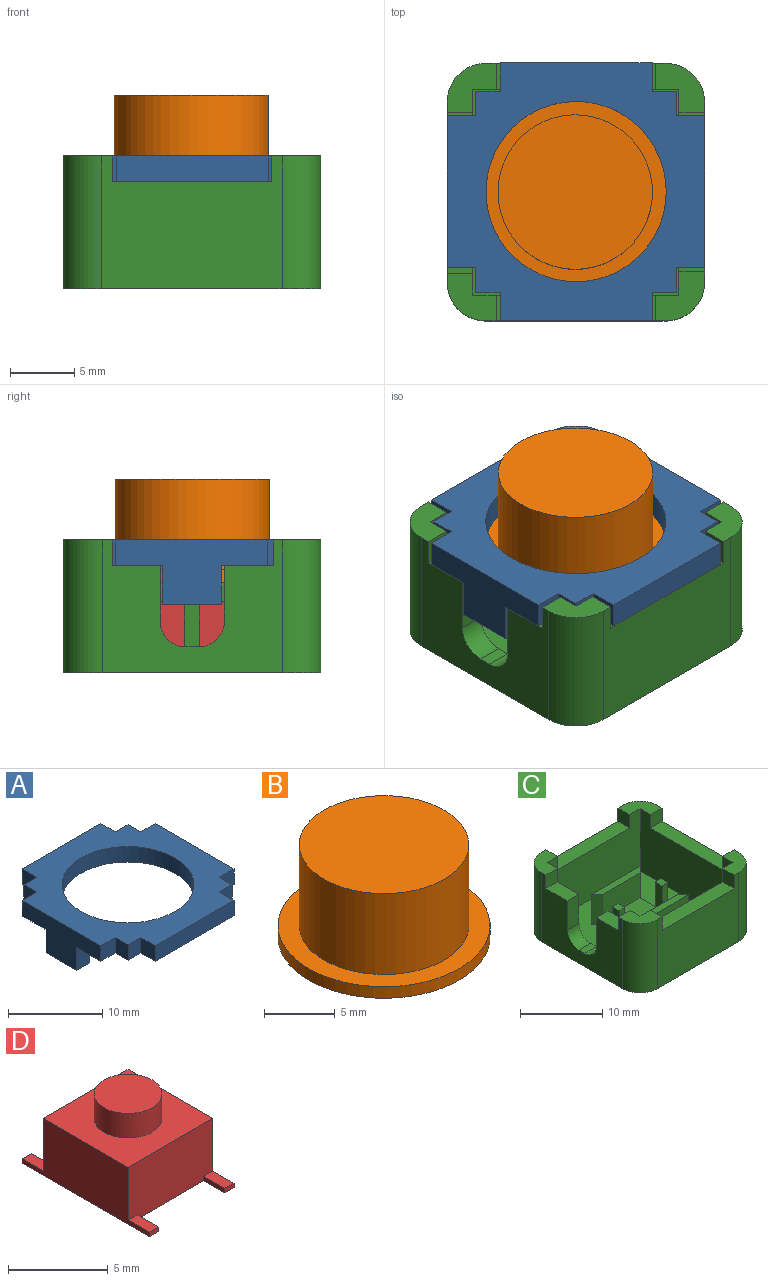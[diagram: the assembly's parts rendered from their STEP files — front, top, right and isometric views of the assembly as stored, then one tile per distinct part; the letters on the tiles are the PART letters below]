
ASSEMBLY  parts=4 mates=3
PART A: 27 faces, bbox 20x20x5 mm
  f0: plane 11.8x2mm, normal (0,1,0), area 23.6mm2, adj f4,f5,f18,f22
  f1: plane 11.8x5mm, normal (-1,0,0), area 37.4mm2, adj f4,f5,f13,f15,f23,f25,f26
  f2: plane 11.8x2mm, normal (0,-1,0), area 23.6mm2, adj f4,f5,f7,f14
  f3: plane 11.8x2mm, normal (1,0,0), area 23.6mm2, adj f4,f5,f8,f21
  f4: plane 20x20mm, normal (0,0,1), area 193.3mm2, adj f0,f1,f2,f3,f6,f7,f8,f9
  f5: plane 20x20mm, normal (0,0,-1), area 184.1mm2, adj f0,f1,f2,f3,f6,f7,f8,f9
  f6: cylinder r=7mm len=14mm, axis (0,0,-1), area 88mm2, adj f4,f5
  f7: plane 2.2x2mm, normal (1,0,0), area 4.4mm2, adj f2,f4,f5,f10
  f8: plane 2.2x2mm, normal (0,-1,0), area 4.4mm2, adj f3,f4,f5,f9
  f9: plane 2x1.9mm, normal (1,0,0), area 3.8mm2, adj f4,f5,f8,f10
  f10: plane 2x1.9mm, normal (0,-1,0), area 3.8mm2, adj f4,f5,f7,f9
  f11: plane 2x1.9mm, normal (0,-1,0), area 3.8mm2, adj f4,f5,f12,f14
  f12: plane 2x1.9mm, normal (-1,0,0), area 3.8mm2, adj f4,f5,f11,f13
  f13: plane 2.2x2mm, normal (0,-1,0), area 4.4mm2, adj f1,f4,f5,f12
  f14: plane 2.2x2mm, normal (-1,0,0), area 4.4mm2, adj f2,f4,f5,f11
  f15: plane 2.2x2mm, normal (0,1,0), area 4.4mm2, adj f1,f4,f5,f16
  f16: plane 2x1.9mm, normal (-1,0,0), area 3.8mm2, adj f4,f5,f15,f17
  f17: plane 2x1.9mm, normal (0,1,0), area 3.8mm2, adj f4,f5,f16,f18
  f18: plane 2.2x2mm, normal (-1,0,0), area 4.4mm2, adj f0,f4,f5,f17
  f19: plane 2x1.9mm, normal (0,1,0), area 3.8mm2, adj f4,f5,f20,f22
  f20: plane 2x1.9mm, normal (1,0,0), area 3.8mm2, adj f4,f5,f19,f21
  f21: plane 2.2x2mm, normal (0,1,0), area 4.4mm2, adj f3,f4,f5,f20
  f22: plane 2.2x2mm, normal (1,0,0), area 4.4mm2, adj f0,f4,f5,f19
  f23: plane 3x2mm, normal (0,1,0), area 6mm2, adj f1,f5,f24,f26
  f24: plane 4.6x3mm, normal (1,0,0), area 13.8mm2, adj f5,f23,f25,f26
  f25: plane 3x2mm, normal (0,-1,0), area 6mm2, adj f1,f5,f24,f26
  f26: plane 4.6x2mm, normal (0,0,-1), area 9.2mm2, adj f1,f23,f24,f25
PART B: 5 faces, bbox 15x15x8 mm
  f0: cylinder r=7.5mm len=15mm, axis (0,0,-1), area 47.1mm2, adj f1,f2
  f1: plane 15x15mm, normal (0,0,1), area 63.6mm2, adj f0,f3
  f2: plane 15x15mm, normal (0,0,-1), area 176.7mm2, adj f0
  f3: cylinder r=6mm len=12mm, axis (0,0,-1), area 263.9mm2, adj f1,f4
  f4: plane 12x12mm, normal (0,0,1), area 113.1mm2, adj f3
PART C: 61 faces, bbox 20x20x10.3 mm
  f0: plane 3.8x2mm, normal (0,0,1), area 7.6mm2, adj f1,f32,f40,f57
  f1: plane 14x10.3mm, normal (-1,0,0), area 89.4mm2, adj f0,f5,f36,f40,f42,f44,f45,f52
  f2: plane 12.4x2mm, normal (0,0,1), area 24.8mm2, adj f35,f38,f41,f50
  f3: plane 12.4x2mm, normal (0,0,1), area 24.8mm2, adj f34,f37,f47,f49
  f4: plane 12.4x2mm, normal (0,0,1), area 24.8mm2, adj f33,f39,f43,f46
  f5: plane 3.7x2mm, normal (0,0,1), area 7.4mm2, adj f1,f32,f44,f58
  f6: plane 16x16mm, normal (0,0,1), area 202.8mm2, adj f7,f8,f9,f10,f12,f13,f14,f15
  f7: plane 6x1mm, normal (0,1,0), area 6mm2, adj f6,f8,f10,f11
  f8: plane 6x1mm, normal (-1,0,0), area 6mm2, adj f6,f7,f9,f11
  f9: plane 6x1mm, normal (0,-1,0), area 6mm2, adj f6,f8,f10,f11
  f10: plane 6x1mm, normal (1,0,0), area 6mm2, adj f6,f7,f9,f11
  f11: plane 6x6mm, normal (0,0,1), area 36mm2, adj f7,f8,f9,f10
  f12: plane 8.4x4.5mm, normal (0,1,0), area 37.8mm2, adj f6,f13,f15,f16
  f13: plane 4.5x1mm, normal (-0.71,-0.71,0), area 6.4mm2, adj f6,f12,f14,f16
  f14: plane 6.4x4.5mm, normal (0,-1,0), area 28.8mm2, adj f6,f13,f15,f16
  f15: plane 4.5x1mm, normal (0.71,-0.71,0), area 6.4mm2, adj f6,f12,f14,f16
  f16: plane 8.4x1mm, normal (0,0,1), area 7.4mm2, adj f12,f13,f14,f15
  f17: plane 8.4x4.5mm, normal (0,-1,0), area 37.8mm2, adj f6,f18,f20,f21
  f18: plane 4.5x1mm, normal (0.71,0.71,0), area 6.4mm2, adj f6,f17,f19,f21
  f19: plane 6.4x4.5mm, normal (0,1,0), area 28.8mm2, adj f6,f18,f20,f21
  f20: plane 4.5x1mm, normal (-0.71,0.71,0), area 6.4mm2, adj f6,f17,f19,f21
  f21: plane 8.4x1mm, normal (0,0,1), area 7.4mm2, adj f17,f18,f19,f20
  f22: plane 4.5x1mm, normal (0,1,0), area 4.5mm2, adj f6,f23,f25,f26
  f23: plane 4.5x1.2mm, normal (-1,0,0), area 5.4mm2, adj f6,f22,f24,f26
  f24: plane 4.5x1mm, normal (0,-1,0), area 4.5mm2, adj f6,f23,f25,f26
  f25: plane 4.5x1.2mm, normal (1,0,0), area 5.4mm2, adj f6,f22,f24,f26
  f26: plane 1.2x1mm, normal (0,0,1), area 1.2mm2, adj f22,f23,f24,f25
  f27: plane 4.5x1mm, normal (0,1,0), area 4.5mm2, adj f6,f28,f30,f31
  f28: plane 4.5x1.2mm, normal (-1,0,0), area 5.4mm2, adj f6,f27,f29,f31
  f29: plane 4.5x1mm, normal (0,-1,0), area 4.5mm2, adj f6,f28,f30,f31
  f30: plane 4.5x1.2mm, normal (1,0,0), area 5.4mm2, adj f6,f27,f29,f31
  f31: plane 1.2x1mm, normal (0,0,1), area 1.2mm2, adj f27,f28,f29,f30
  f32: plane 16x9.3mm, normal (1,0,0), area 94mm2, adj f0,f5,f6,f33,f35,f40,f42,f44
  f33: plane 16x9.3mm, normal (0,-1,0), area 124mm2, adj f4,f6,f32,f34,f43,f45,f46,f48
  f34: plane 16x9.3mm, normal (-1,0,0), area 124mm2, adj f3,f6,f33,f35,f47,f48,f49,f51
  f35: plane 16x9.3mm, normal (0,1,0), area 124mm2, adj f2,f6,f32,f34,f41,f42,f50,f51
  f36: plane 20x20mm, normal (0,0,-1), area 392.3mm2, adj f1,f37,f38,f39,f52,f53,f54,f55
  f37: plane 14x10.3mm, normal (1,0,0), area 119.4mm2, adj f3,f36,f47,f48,f49,f51,f54,f55
  f38: plane 14x10.3mm, normal (0,-1,0), area 119.4mm2, adj f2,f36,f41,f42,f50,f51,f53,f54
  f39: plane 14x10.3mm, normal (0,1,0), area 119.4mm2, adj f4,f36,f43,f45,f46,f48,f52,f55
  f40: plane 2x2mm, normal (0,1,0), area 4mm2, adj f0,f1,f32,f42
  f41: plane 2x2mm, normal (1,0,0), area 4mm2, adj f2,f35,f38,f42
  f42: plane 3.8x3.7mm, normal (0,0,1), area 9.1mm2, adj f1,f32,f35,f38,f40,f41,f53
  f43: plane 2x2mm, normal (1,0,0), area 4mm2, adj f4,f33,f39,f45
  f44: plane 2x2mm, normal (0,-1,0), area 4mm2, adj f1,f5,f32,f45
  f45: plane 3.8x3.8mm, normal (0,0,1), area 9.3mm2, adj f1,f32,f33,f39,f43,f44,f52
  f46: plane 2x2mm, normal (-1,0,0), area 4mm2, adj f4,f33,f39,f48
  f47: plane 2x2mm, normal (0,-1,0), area 4mm2, adj f3,f34,f37,f48
  f48: plane 3.8x3.8mm, normal (0,0,1), area 9.3mm2, adj f33,f34,f37,f39,f46,f47,f55
  f49: plane 2x2mm, normal (0,1,0), area 4mm2, adj f3,f34,f37,f51
  f50: plane 2x2mm, normal (-1,0,0), area 4mm2, adj f2,f35,f38,f51
  f51: plane 3.8x3.8mm, normal (0,0,1), area 9.3mm2, adj f34,f35,f37,f38,f49,f50,f54
  f52: cylinder r=3mm len=10.3mm, axis (0,0,1), area 48.5mm2, adj f1,f36,f39,f45
  f53: cylinder r=3mm len=10.3mm, axis (0,0,-1), area 48.5mm2, adj f1,f36,f38,f42
  f54: cylinder r=3mm len=10.3mm, axis (0,0,1), area 48.5mm2, adj f36,f37,f38,f51
  f55: cylinder r=3mm len=10.3mm, axis (0,0,-1), area 48.5mm2, adj f36,f37,f39,f48
  f56: plane 2x1mm, normal (0,0,1), area 2mm2, adj f1,f32,f59,f60
  f57: plane 4.3x2mm, normal (0,1,0), area 8.6mm2, adj f0,f1,f32,f59
  f58: plane 4.3x2mm, normal (0,-1,0), area 8.6mm2, adj f1,f5,f32,f60
  f59: cylinder r=2mm len=2mm, axis (-1,0,0), area 6.3mm2, adj f1,f32,f56,f57
  f60: cylinder r=2mm len=2mm, axis (1,0,0), area 6.3mm2, adj f1,f32,f56,f58
PART D: 20 faces, bbox 6x9x5 mm
  f0: plane 6x3.5mm, normal (0,-1,0), area 20.7mm2, adj f2,f3,f4,f5,f9,f10,f11,f13
  f1: plane 6x3.5mm, normal (0,1,0), area 20.7mm2, adj f2,f3,f4,f5,f15,f16,f17,f19
  f2: plane 9x3.5mm, normal (-1,0,0), area 21.8mm2, adj f0,f1,f4,f5,f12,f13,f14,f16
  f3: plane 9x3.5mm, normal (1,0,0), area 21.8mm2, adj f0,f1,f4,f5,f8,f10,f18,f19
  f4: plane 6x6mm, normal (0,0,1), area 26.9mm2, adj f0,f1,f2,f3,f6
  f5: plane 9x6mm, normal (0,0,-1), area 39.8mm2, adj f0,f1,f2,f3,f8,f9,f11,f12
  f6: cylinder r=1.7mm len=3.4mm, axis (0,0,-1), area 16mm2, adj f4,f7
  f7: plane 3.4x3.4mm, normal (0,0,1), area 9.1mm2, adj f6
  f8: plane 0.64x0.27mm, normal (0,-1,0), area 0.2mm2, adj f3,f5,f9,f10
  f9: plane 1.5x0.27mm, normal (-1,0,0), area 0.4mm2, adj f0,f5,f8,f10
  f10: plane 1.5x0.64mm, normal (0,0,1), area 1mm2, adj f0,f3,f8,f9
  f11: plane 1.5x0.27mm, normal (1,0,0), area 0.4mm2, adj f0,f5,f12,f13
  f12: plane 0.64x0.27mm, normal (0,-1,0), area 0.2mm2, adj f2,f5,f11,f13
  f13: plane 1.5x0.64mm, normal (0,0,1), area 1mm2, adj f0,f2,f11,f12
  f14: plane 0.64x0.27mm, normal (0,1,0), area 0.2mm2, adj f2,f5,f15,f16
  f15: plane 1.5x0.27mm, normal (1,0,0), area 0.4mm2, adj f1,f5,f14,f16
  f16: plane 1.5x0.64mm, normal (0,0,1), area 1mm2, adj f1,f2,f14,f15
  f17: plane 1.5x0.27mm, normal (-1,0,0), area 0.4mm2, adj f1,f5,f18,f19
  f18: plane 0.64x0.27mm, normal (0,1,0), area 0.2mm2, adj f3,f5,f17,f19
  f19: plane 1.5x0.64mm, normal (0,0,1), area 1mm2, adj f1,f3,f17,f18
PLACE A t=(1.54,1.7,-1.58)mm
PLACE B t=(-1.52,4.66,0.42)mm
PLACE C t=(1.53,1.66,-1.58)mm fixed
PLACE D rot(axis=(0,0,1),90deg) t=(-1.52,-1.34,0.42)mm
MATE planar A.f5 <-> C.f4  axis (0,0,-1) through (1.99,1.7,6.72)mm
MATE planar B.f0 <-> D.f6  axis (0,0,-1) through (1.48,1.66,5.42)mm
MATE planar D.f6 <-> C.f11  axis (0,0,-1) through (1.48,1.66,0.42)mm
